# Revit family: HP DXE R1000
name_source: partatom
category: Mechanical Equipment
revit_build: Autodesk Revit 2015 (Build: 20140606_1530(x64)
units: mm (PartAtom-declared; Revit-internal decimal feet)

## types (4) — shared parameters
Center X = 805 mm
Center X1 = 790 mm
Center Y = 177 mm
Center Y1 = 151 mm
Colour = As standard white RAL (9010) but this can be changed upon purchase.
Fan type = AC ELCOfan deck
ISO 27327 uniformity at outlet = 90%
Loading (A) per phase = 0.8 or (7.3)
Manufacturer = Thermoscreens
Maxium likely condensate flow rate (litres/hours) = 6.0
Noise output dB (A) @3m low = 47
Number of hanging points = 4
Product URL = http://www.thermoscreens.com
Supply (50Hz) = 230V~1P&N
Temerature classification = low temperature
URL = http://www.thermoscreens.com
Version = 1.0
Weight (kg) = 52kg
maximum mounting height of air curtain = 3.8m
meathord of mesurement = mm unless stated different in the parameter

## per-type parameters (varying)
| type | Air volume@(m3/h) high | Air volume@(m3/h) low | Air volume@(m3/h) medium | Description | Effective width of air stream | Material | Max.DX heat output | Maxium air volume flow rate (m3/H) | Maxium cooling output (kW) | Maxium heating output(kW) | Model | Model reference | Noise output dB (A) @3m high | Noise output dB (A) @3m med | Rated current (A) | Rated electrial power input (kW) | VRF index system |
| HP DXE1000 MR SLIM AC | 1310 | 900 | 1170 |  | 1.10 | sheet steel | 8.3 with P71 unit | 1310 | 7.4 | 8.3 | HP DXE 1000 MR SLIM AC ELCO FANDECK | HP DXE 1000 MR SLIM AC | 57 | 54 | 0.8 | 0.2 |  |
| HP DXE 1000 MR SLIM EC | 1510 | 920 | 1240 | the HP DXE is our leading product on heat pump. this air curtain is good for | 1.18 | sheet steel 20 gauge | 8.9with P71 unit | 1590 | 7.8 | 8.9 | HP DXE 1000 MR SLIM AC ELCO FANDECK | HP DXE 1000 MR SLIM AC | 58 | 55 | 1.2 | 0.3 |  |
| HP DXE 1000R VRF AC | 1510 | 920 | 1240 | the HP DXE is our leading product on heat pump. this air curtain is good for | 1.18 | sheet steel 20 gauge | 8.3 with P71 unit | 1310 | 7.4 | 8.9 | HP DXE 1000R MR SLIM AC ELCO FANDECK | HP DXE 1000R MR SLIM AC | 58 | 55 | 1.2 | 0.2 |  |
| HP DXE 1000R VRF EC | 1510 | 920 | 1240 | the HP DXE is our leading product on heat pump. this air curtain is good for | 1.18 | sheet steel 20 gauge | 8.9 with P71 unit | 1530 | 7.8 | 8.9 | HP DXE 1000R MR SLIM AC ELCO FANDECK | HP DXE 1000R MR SLIM AC | 58 | 55 | 1.3 | 0.3 | P71 |

## geometry (parser evidence)
native form markers: Sweep x2
no freeform markers — native parametric forms only
